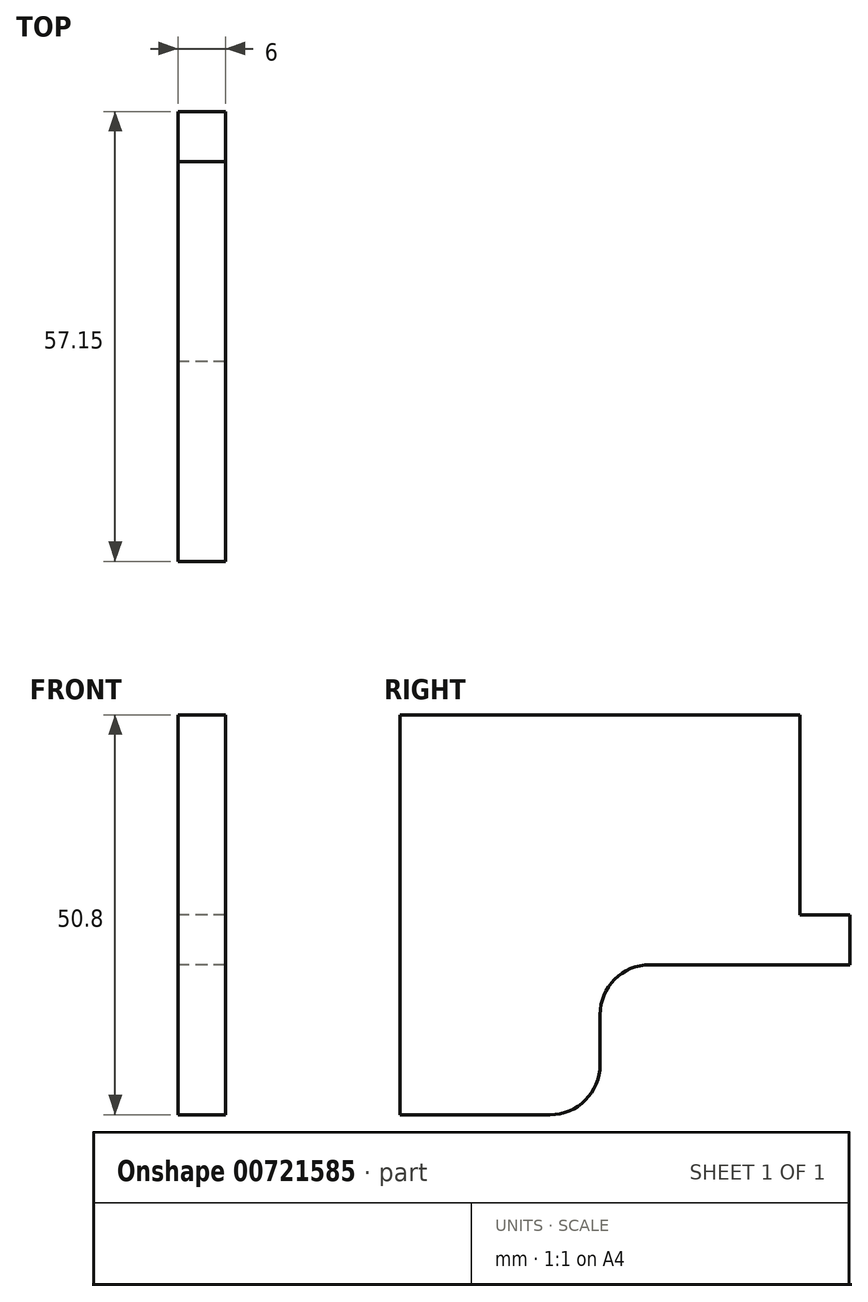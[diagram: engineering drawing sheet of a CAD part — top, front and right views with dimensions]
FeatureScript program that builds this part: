
annotation { "Feature Type Name" : "Feature", "Feature Type Description" : "" }
export const myFeature = defineFeature(function(context is Context, id is Id, definition is map)
    precondition{}
    {
        {
            var Q0;
            Q0=qCreatedBy(makeId("Right.planeOp"),FACE);
            var sketch = newSketch(context, id + "F0", { "sketchPlane" : qUnion([Q0])});
            skLineSegment(sketch, "E0", {"start": v(0, 0) * mm, "end": v(0, 50.8) * mm});
            skLineSegment(sketch, "E1", {"start": v(0, 50.8) * mm, "end": v(50.8, 50.8) * mm});
            skLineSegment(sketch, "E2", {"start": v(50.8, 50.8) * mm, "end": v(50.8, 25.4) * mm});
            skLineSegment(sketch, "E3", {"start": v(50.8, 25.4) * mm, "end": v(57.15, 25.4) * mm});
            skLineSegment(sketch, "E4", {"start": v(57.15, 25.4) * mm, "end": v(57.15, 19.05) * mm});
            skLineSegment(sketch, "E5", {"start": v(57.15, 19.05) * mm, "end": v(31.75, 19.05) * mm});
            skLineSegment(sketch, "E6", {"start": v(25.4, 12.7) * mm, "end": v(25.4, 6.35) * mm});
            skLineSegment(sketch, "E7", {"start": v(19.05, 0) * mm, "end": v(0, 0) * mm});
            skPoint(sketch, "E8.visualSharp", {"position": v(25.4, 0) * mm});
            skArc(sketch, "E8.filletArc", {"start": v(19.05, 0) * mm, "mid": v(23.54, 1.86) * mm, "end": v(25.4, 6.35) * mm});
            skPoint(sketch, "E9.visualSharp", {"position": v(25.4, 19.05) * mm});
            skArc(sketch, "E9.filletArc", {"start": v(31.75, 19.05) * mm, "mid": v(27.26, 17.2) * mm, "end": v(25.4, 12.7) * mm});
            skSolve(sketch);
        }
        {
            var Q0;
            Q0=makeQuery(id+"F0.imprint","IMPRINT",FACE,{"disambiguationData":[TD([[makeQuery(id+"F0.imprint","IMPRINT",EDGE,{"derivedFrom":sQuery(id+"F0.wireOp",EDGE,"E0")}),-1.0]])]});
            extrude(context, id + "F1", {"entities" : qUnion([Q0]), "depth" : 6 * mm, "offsetDistance" : 25.4 * mm, "symmetric" : true});
        }
    });
